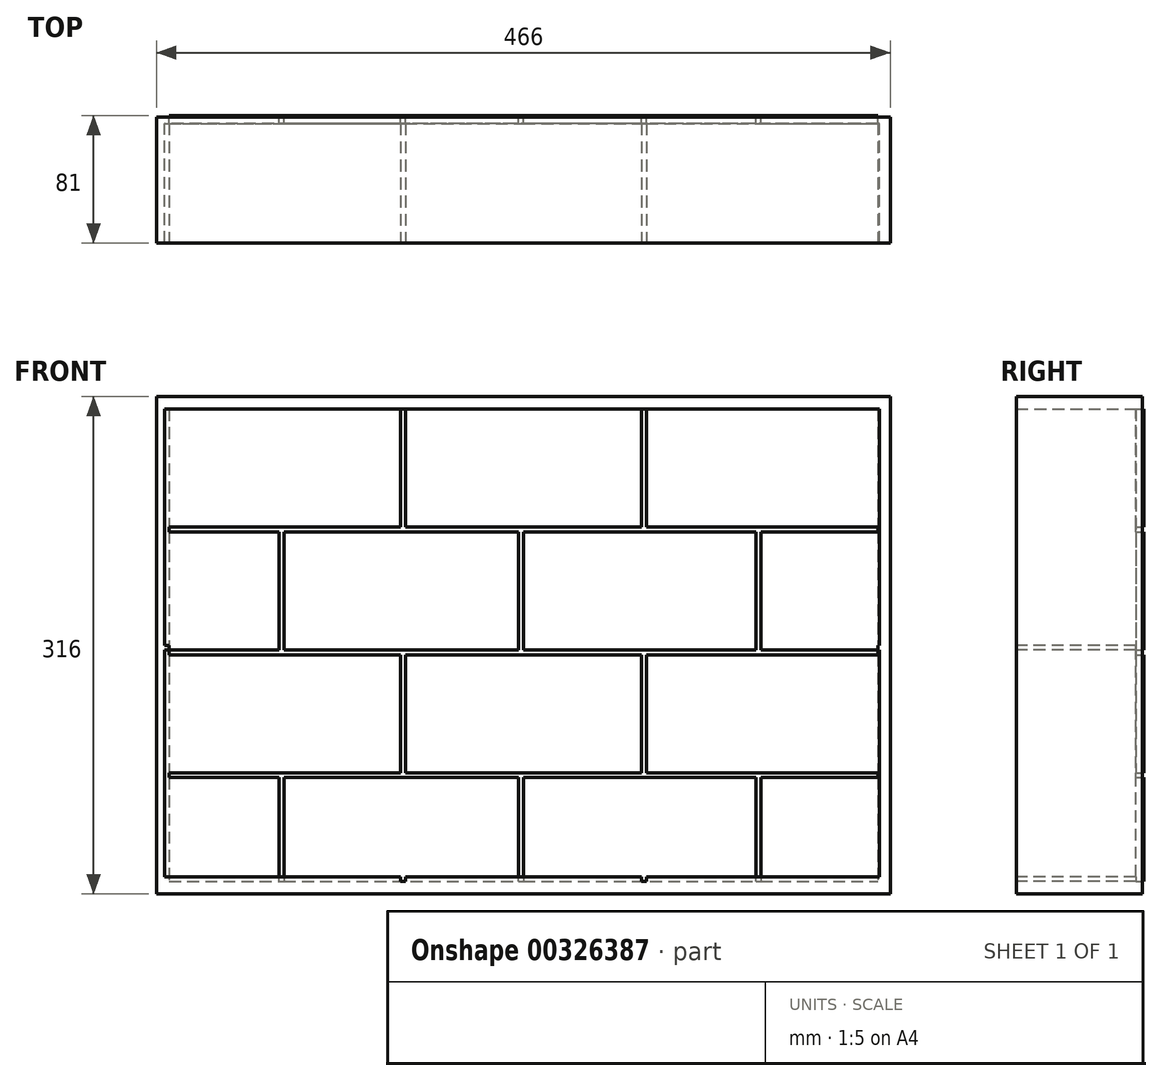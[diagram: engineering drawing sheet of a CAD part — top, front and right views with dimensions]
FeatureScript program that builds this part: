
annotation { "Feature Type Name" : "Feature", "Feature Type Description" : "" }
export const myFeature = defineFeature(function(context is Context, id is Id, definition is map)
    precondition{}
    {
        {
            var Q0;
            Q0=qCreatedBy(makeId("Front.planeOp"),FACE);
            var sketch = newSketch(context, id + "F0", { "sketchPlane" : qUnion([Q0])});
            skLineSegment(sketch, "E0.bottom", {"start": v(0, 300) * mm, "end": v(450, 300) * mm});
            skLineSegment(sketch, "E0.top", {"start": v(0, 0) * mm, "end": v(450, 0) * mm});
            skLineSegment(sketch, "E0.left", {"start": v(0, 300) * mm, "end": v(0, 0) * mm});
            skLineSegment(sketch, "E0.right", {"start": v(450, 300) * mm, "end": v(450, 0) * mm});
            skLineSegment(sketch, "E1.bottom", {"start": v(150, 300) * mm, "end": v(300, 300) * mm});
            skLineSegment(sketch, "E1.top", {"start": v(150, 225) * mm, "end": v(300, 225) * mm});
            skLineSegment(sketch, "E1.left", {"start": v(150, 300) * mm, "end": v(150, 225) * mm});
            skLineSegment(sketch, "E1.right", {"start": v(300, 300) * mm, "end": v(300, 225) * mm});
            skLineSegment(sketch, "E2.bottom", {"start": v(147, 300) * mm, "end": v(0, 300) * mm});
            skLineSegment(sketch, "E2.top", {"start": v(147, 225) * mm, "end": v(0, 225) * mm});
            skLineSegment(sketch, "E2.left", {"start": v(147, 300) * mm, "end": v(147, 225) * mm});
            skLineSegment(sketch, "E2.right", {"start": v(0, 300) * mm, "end": v(0, 225) * mm});
            skLineSegment(sketch, "E3.bottom", {"start": v(303, 300) * mm, "end": v(450, 300) * mm});
            skLineSegment(sketch, "E3.top", {"start": v(303, 225) * mm, "end": v(450, 225) * mm});
            skLineSegment(sketch, "E3.left", {"start": v(303, 300) * mm, "end": v(303, 225) * mm});
            skLineSegment(sketch, "E3.right", {"start": v(450, 300) * mm, "end": v(450, 225) * mm});
            skLineSegment(sketch, "E4", {"start": v(225, 300) * mm, "end": v(225, 0) * mm, "construction": true});
            skLineSegment(sketch, "E5.bottom", {"start": v(72.9, 222) * mm, "end": v(222, 222) * mm});
            skLineSegment(sketch, "E5.top", {"start": v(72.9, 147) * mm, "end": v(222, 147) * mm});
            skLineSegment(sketch, "E5.left", {"start": v(72.9, 222) * mm, "end": v(72.9, 147) * mm});
            skLineSegment(sketch, "E5.right", {"start": v(222, 222) * mm, "end": v(222, 147) * mm});
            skLineSegment(sketch, "E6.bottom", {"start": v(225, 222) * mm, "end": v(372.78, 222) * mm});
            skLineSegment(sketch, "E6.top", {"start": v(225, 147) * mm, "end": v(372.78, 147) * mm});
            skLineSegment(sketch, "E6.left", {"start": v(225, 222) * mm, "end": v(225, 147) * mm});
            skLineSegment(sketch, "E6.right", {"start": v(372.78, 222) * mm, "end": v(372.78, 147) * mm});
            skLineSegment(sketch, "E7.bottom", {"start": v(375.78, 222) * mm, "end": v(450, 222) * mm});
            skLineSegment(sketch, "E7.top", {"start": v(375.78, 147) * mm, "end": v(450, 147) * mm});
            skLineSegment(sketch, "E7.left", {"start": v(375.78, 222) * mm, "end": v(375.78, 147) * mm});
            skLineSegment(sketch, "E7.right", {"start": v(450, 222) * mm, "end": v(450, 147) * mm});
            skLineSegment(sketch, "E8.bottom", {"start": v(0, 222) * mm, "end": v(69.9, 222) * mm});
            skLineSegment(sketch, "E8.top", {"start": v(0, 147) * mm, "end": v(69.9, 147) * mm});
            skLineSegment(sketch, "E8.left", {"start": v(0, 222) * mm, "end": v(0, 147) * mm});
            skLineSegment(sketch, "E8.right", {"start": v(69.9, 222) * mm, "end": v(69.9, 147) * mm});
            skLineSegment(sketch, "E9.bottom", {"start": v(150, 144) * mm, "end": v(300, 144) * mm});
            skLineSegment(sketch, "E9.top", {"start": v(150, 69) * mm, "end": v(300, 69) * mm});
            skLineSegment(sketch, "E9.left", {"start": v(150, 144) * mm, "end": v(150, 69) * mm});
            skLineSegment(sketch, "E9.right", {"start": v(300, 144) * mm, "end": v(300, 69) * mm});
            skLineSegment(sketch, "E10.bottom", {"start": v(303, 144) * mm, "end": v(450, 144) * mm});
            skLineSegment(sketch, "E10.top", {"start": v(303, 69) * mm, "end": v(450, 69) * mm});
            skLineSegment(sketch, "E10.left", {"start": v(303, 144) * mm, "end": v(303, 69) * mm});
            skLineSegment(sketch, "E10.right", {"start": v(450, 144) * mm, "end": v(450, 69) * mm});
            skLineSegment(sketch, "E11.bottom", {"start": v(0, 69) * mm, "end": v(147, 69) * mm});
            skLineSegment(sketch, "E11.top", {"start": v(0, 144) * mm, "end": v(147, 144) * mm});
            skLineSegment(sketch, "E11.left", {"start": v(0, 69) * mm, "end": v(0, 144) * mm});
            skLineSegment(sketch, "E11.right", {"start": v(147, 69) * mm, "end": v(147, 144) * mm});
            skLineSegment(sketch, "E12.bottom", {"start": v(0, 66) * mm, "end": v(69.9, 66) * mm});
            skLineSegment(sketch, "E12.top", {"start": v(0, 0) * mm, "end": v(69.9, 0) * mm});
            skLineSegment(sketch, "E12.left", {"start": v(0, 66) * mm, "end": v(0, 0) * mm});
            skLineSegment(sketch, "E12.right", {"start": v(69.9, 66) * mm, "end": v(69.9, 0) * mm});
            skLineSegment(sketch, "E13.bottom", {"start": v(72.9, 66) * mm, "end": v(222, 66) * mm});
            skLineSegment(sketch, "E13.top", {"start": v(72.9, 0) * mm, "end": v(222, 0) * mm});
            skLineSegment(sketch, "E13.left", {"start": v(72.9, 66) * mm, "end": v(72.9, 0) * mm});
            skLineSegment(sketch, "E13.right", {"start": v(222, 66) * mm, "end": v(222, 0) * mm});
            skLineSegment(sketch, "E14.bottom", {"start": v(225, 66) * mm, "end": v(372.78, 66) * mm});
            skLineSegment(sketch, "E14.top", {"start": v(225, 0) * mm, "end": v(372.78, 0) * mm});
            skLineSegment(sketch, "E14.left", {"start": v(225, 66) * mm, "end": v(225, 0) * mm});
            skLineSegment(sketch, "E14.right", {"start": v(372.78, 66) * mm, "end": v(372.78, 0) * mm});
            skLineSegment(sketch, "E15.bottom", {"start": v(375.78, 66) * mm, "end": v(450, 66) * mm});
            skLineSegment(sketch, "E15.top", {"start": v(375.78, 0) * mm, "end": v(450, 0) * mm});
            skLineSegment(sketch, "E15.left", {"start": v(375.78, 66) * mm, "end": v(375.78, 0) * mm});
            skLineSegment(sketch, "E15.right", {"start": v(450, 66) * mm, "end": v(450, 0) * mm});
            skLineSegment(sketch, "E16.bottom", {"start": v(-8, 308) * mm, "end": v(458, 308) * mm});
            skLineSegment(sketch, "E16.top", {"start": v(-8, -8) * mm, "end": v(458, -8) * mm});
            skLineSegment(sketch, "E16.left", {"start": v(-8, 308) * mm, "end": v(-8, -8) * mm});
            skLineSegment(sketch, "E16.right", {"start": v(458, 308) * mm, "end": v(458, -8) * mm});
            skSolve(sketch);
        }
        {
            var Q0;
            Q0=qCreatedBy(makeId("Front.planeOp"),FACE);
            cPlane(context, id + "F1", {"entities" : qUnion([Q0]), "cplaneType" : CPlaneType.OFFSET, "offset" : 78 * mm, "width" : 150 * mm, "height" : 150 * mm});
        }
        {
            var Q0;
            Q0=qCreatedBy(id+"F1.planeOp",FACE);
            var sketch = newSketch(context, id + "F2", { "sketchPlane" : qUnion([Q0])});
            skLineSegment(sketch, "E17.0", {"start": v(-8, 308) * mm, "end": v(-8, -8) * mm});
            skLineSegment(sketch, "E17.1", {"start": v(-8, 308) * mm, "end": v(458, 308) * mm});
            skLineSegment(sketch, "E17.2", {"start": v(458, 308) * mm, "end": v(458, -8) * mm});
            skLineSegment(sketch, "E17.3", {"start": v(-8, -8) * mm, "end": v(458, -8) * mm});
            skLineSegment(sketch, "E18.0", {"start": v(0, 300) * mm, "end": v(450, 300) * mm});
            skLineSegment(sketch, "E18.1", {"start": v(0, 300) * mm, "end": v(0, 0) * mm});
            skLineSegment(sketch, "E18.2", {"start": v(0, 0) * mm, "end": v(450, 0) * mm});
            skLineSegment(sketch, "E18.3", {"start": v(450, 300) * mm, "end": v(450, 0) * mm});
            skSolve(sketch);
        }
        {
            var Q0;
            Q0 = qSketchRegion(id + "F2", true);
            extrude(context, id + "F3", {"entities" : qUnion([Q0]), "depth" : 3 * mm, "offsetDistance" : 25 * mm, "hasSecondDirection" : true, "secondDirectionOppositeDirection" : true, "secondDirectionDepth" : 77 * mm});
        }
        {
            var Q0;
            Q0=qCreatedBy(makeId("Front.planeOp"),FACE);
            var sketch = newSketch(context, id + "F4", { "sketchPlane" : qUnion([Q0])});
            skLineSegment(sketch, "E19.0.0", {"start": v(147, 225) * mm, "end": v(147, 300) * mm});
            skLineSegment(sketch, "E19.0.1", {"start": v(147, 300) * mm, "end": v(0, 300) * mm});
            skLineSegment(sketch, "E19.0.2", {"start": v(0, 300) * mm, "end": v(0, 225) * mm});
            skLineSegment(sketch, "E19.0.3", {"start": v(0, 225) * mm, "end": v(147, 225) * mm});
            skLineSegment(sketch, "E20.0.0", {"start": v(300, 225) * mm, "end": v(300, 300) * mm});
            skLineSegment(sketch, "E20.0.1", {"start": v(300, 300) * mm, "end": v(150, 300) * mm});
            skLineSegment(sketch, "E20.0.2", {"start": v(150, 300) * mm, "end": v(150, 225) * mm});
            skLineSegment(sketch, "E20.0.3", {"start": v(150, 225) * mm, "end": v(300, 225) * mm});
            skLineSegment(sketch, "E21.0.0", {"start": v(450, 300) * mm, "end": v(303, 300) * mm});
            skLineSegment(sketch, "E21.0.1", {"start": v(303, 300) * mm, "end": v(303, 225) * mm});
            skLineSegment(sketch, "E21.0.2", {"start": v(303, 225) * mm, "end": v(450, 225) * mm});
            skLineSegment(sketch, "E21.0.3", {"start": v(450, 225) * mm, "end": v(450, 300) * mm});
            skLineSegment(sketch, "E22.0.0", {"start": v(69.9, 222) * mm, "end": v(0, 222) * mm});
            skLineSegment(sketch, "E22.0.1", {"start": v(0, 222) * mm, "end": v(0, 147) * mm});
            skLineSegment(sketch, "E22.0.2", {"start": v(0, 147) * mm, "end": v(69.9, 147) * mm});
            skLineSegment(sketch, "E22.0.3", {"start": v(69.9, 147) * mm, "end": v(69.9, 222) * mm});
            skLineSegment(sketch, "E23.0.0", {"start": v(72.9, 222) * mm, "end": v(72.9, 147) * mm});
            skLineSegment(sketch, "E23.0.1", {"start": v(72.9, 147) * mm, "end": v(222, 147) * mm});
            skLineSegment(sketch, "E23.0.2", {"start": v(222, 147) * mm, "end": v(222, 222) * mm});
            skLineSegment(sketch, "E23.0.3", {"start": v(222, 222) * mm, "end": v(72.9, 222) * mm});
            skLineSegment(sketch, "E24.0.0", {"start": v(225, 222) * mm, "end": v(225, 147) * mm});
            skLineSegment(sketch, "E24.0.1", {"start": v(225, 147) * mm, "end": v(372.78, 147) * mm});
            skLineSegment(sketch, "E24.0.2", {"start": v(372.78, 147) * mm, "end": v(372.78, 222) * mm});
            skLineSegment(sketch, "E24.0.3", {"start": v(372.78, 222) * mm, "end": v(225, 222) * mm});
            skLineSegment(sketch, "E25.0.0", {"start": v(450, 147) * mm, "end": v(450, 222) * mm});
            skLineSegment(sketch, "E25.0.1", {"start": v(450, 222) * mm, "end": v(375.78, 222) * mm});
            skLineSegment(sketch, "E25.0.2", {"start": v(375.78, 222) * mm, "end": v(375.78, 147) * mm});
            skLineSegment(sketch, "E25.0.3", {"start": v(375.78, 147) * mm, "end": v(450, 147) * mm});
            skLineSegment(sketch, "E26.0.0", {"start": v(450, 69) * mm, "end": v(450, 144) * mm});
            skLineSegment(sketch, "E26.0.1", {"start": v(450, 144) * mm, "end": v(303, 144) * mm});
            skLineSegment(sketch, "E26.0.2", {"start": v(303, 144) * mm, "end": v(303, 69) * mm});
            skLineSegment(sketch, "E26.0.3", {"start": v(303, 69) * mm, "end": v(450, 69) * mm});
            skLineSegment(sketch, "E27.0.0", {"start": v(150, 144) * mm, "end": v(150, 69) * mm});
            skLineSegment(sketch, "E27.0.1", {"start": v(150, 69) * mm, "end": v(300, 69) * mm});
            skLineSegment(sketch, "E27.0.2", {"start": v(300, 69) * mm, "end": v(300, 144) * mm});
            skLineSegment(sketch, "E27.0.3", {"start": v(300, 144) * mm, "end": v(150, 144) * mm});
            skLineSegment(sketch, "E28.0.0", {"start": v(0, 144) * mm, "end": v(0, 69) * mm});
            skLineSegment(sketch, "E28.0.1", {"start": v(0, 69) * mm, "end": v(147, 69) * mm});
            skLineSegment(sketch, "E28.0.2", {"start": v(147, 69) * mm, "end": v(147, 144) * mm});
            skLineSegment(sketch, "E28.0.3", {"start": v(147, 144) * mm, "end": v(0, 144) * mm});
            skLineSegment(sketch, "E29.0.0", {"start": v(222, 0) * mm, "end": v(222, 66) * mm});
            skLineSegment(sketch, "E29.0.1", {"start": v(222, 66) * mm, "end": v(72.9, 66) * mm});
            skLineSegment(sketch, "E29.0.2", {"start": v(72.9, 66) * mm, "end": v(72.9, 0) * mm});
            skLineSegment(sketch, "E29.0.3", {"start": v(72.9, 0) * mm, "end": v(222, 0) * mm});
            skLineSegment(sketch, "E30.0.0", {"start": v(69.9, 0) * mm, "end": v(69.9, 66) * mm});
            skLineSegment(sketch, "E30.0.1", {"start": v(69.9, 66) * mm, "end": v(0, 66) * mm});
            skLineSegment(sketch, "E30.0.2", {"start": v(0, 66) * mm, "end": v(0, 0) * mm});
            skLineSegment(sketch, "E30.0.3", {"start": v(0, 0) * mm, "end": v(69.9, 0) * mm});
            skLineSegment(sketch, "E31.0.0", {"start": v(372.78, 0) * mm, "end": v(372.78, 66) * mm});
            skLineSegment(sketch, "E31.0.1", {"start": v(372.78, 66) * mm, "end": v(225, 66) * mm});
            skLineSegment(sketch, "E31.0.2", {"start": v(225, 66) * mm, "end": v(225, 0) * mm});
            skLineSegment(sketch, "E31.0.3", {"start": v(225, 0) * mm, "end": v(372.78, 0) * mm});
            skLineSegment(sketch, "E32.0.0", {"start": v(450, 66) * mm, "end": v(375.78, 66) * mm});
            skLineSegment(sketch, "E32.0.1", {"start": v(375.78, 66) * mm, "end": v(375.78, 0) * mm});
            skLineSegment(sketch, "E32.0.2", {"start": v(375.78, 0) * mm, "end": v(450, 0) * mm});
            skLineSegment(sketch, "E32.0.3", {"start": v(450, 0) * mm, "end": v(450, 66) * mm});
            skSolve(sketch);
        }
        {
            var Q0;
            Q0 = qSketchRegion(id + "F4", true);
            extrude(context, id + "F5", {"entities" : qUnion([Q0]), "operationType" : NewBodyOperationType.ADD, "depth" : 5 * mm, "offsetDistance" : 25 * mm});
        }
        {
            var Q0;
            Q0=makeQuery(id+"F3.opExtrude","SWEPT_FACE",FACE,{"disambiguationData":[OSD([sQuery(id+"F2.wireOp",EDGE,"E18.2")])]});
            var sketch = newSketch(context, id + "F6", { "sketchPlane" : qUnion([Q0])});
            skLineSegment(sketch, "E33.0", {"start": v(0, -81) * mm, "end": v(450, -81) * mm, "construction": true});
            skLineSegment(sketch, "E34.bottom", {"start": v(0, -5) * mm, "end": v(147, -5) * mm});
            skLineSegment(sketch, "E34.top", {"start": v(0, -81) * mm, "end": v(147, -81) * mm});
            skLineSegment(sketch, "E34.left", {"start": v(0, -5) * mm, "end": v(0, -81) * mm});
            skLineSegment(sketch, "E34.right", {"start": v(147, -5) * mm, "end": v(147, -81) * mm});
            skLineSegment(sketch, "E35.bottom", {"start": v(150, -5) * mm, "end": v(300, -5) * mm});
            skLineSegment(sketch, "E35.top", {"start": v(150, -81) * mm, "end": v(300, -81) * mm});
            skLineSegment(sketch, "E35.left", {"start": v(150, -5) * mm, "end": v(150, -81) * mm});
            skLineSegment(sketch, "E35.right", {"start": v(300, -5) * mm, "end": v(300, -81) * mm});
            skLineSegment(sketch, "E36.bottom", {"start": v(303, -5) * mm, "end": v(450, -5) * mm});
            skLineSegment(sketch, "E36.top", {"start": v(303, -81) * mm, "end": v(450, -81) * mm});
            skLineSegment(sketch, "E36.left", {"start": v(303, -5) * mm, "end": v(303, -81) * mm});
            skLineSegment(sketch, "E36.right", {"start": v(450, -5) * mm, "end": v(450, -81) * mm});
            skLineSegment(sketch, "E37", {"start": v(225, -81) * mm, "end": v(225, 28.58) * mm, "construction": true});
            skPoint(sketch, "E38", {"position": v(225, -5) * mm});
            skSolve(sketch);
        }
        {
            var Q0;
            Q0 = qSketchRegion(id + "F6", true);
            extrude(context, id + "F7", {"entities" : qUnion([Q0]), "operationType" : NewBodyOperationType.ADD, "depth" : 3 * mm, "offsetDistance" : 25 * mm});
        }
        {
            var Q0;
            Q0=makeQuery(id+"F3.opExtrude","SWEPT_FACE",FACE,{"disambiguationData":[OSD([sQuery(id+"F2.wireOp",EDGE,"E18.1")])]});
            var sketch = newSketch(context, id + "F8", { "sketchPlane" : qUnion([Q0])});
            skLineSegment(sketch, "E39.bottom", {"start": v(-5, 300) * mm, "end": v(-81, 300) * mm});
            skLineSegment(sketch, "E39.top", {"start": v(-5, 150) * mm, "end": v(-81, 150) * mm});
            skLineSegment(sketch, "E39.left", {"start": v(-5, 300) * mm, "end": v(-5, 150) * mm});
            skLineSegment(sketch, "E39.right", {"start": v(-81, 300) * mm, "end": v(-81, 150) * mm});
            skLineSegment(sketch, "E40.bottom", {"start": v(-5, 147) * mm, "end": v(-81, 147) * mm});
            skLineSegment(sketch, "E40.top", {"start": v(-5, 3) * mm, "end": v(-81, 3) * mm});
            skLineSegment(sketch, "E40.left", {"start": v(-5, 147) * mm, "end": v(-5, 3) * mm});
            skLineSegment(sketch, "E40.right", {"start": v(-81, 147) * mm, "end": v(-81, 3) * mm});
            skSolve(sketch);
        }
        {
            var Q0;
            Q0 = qSketchRegion(id + "F8", true);
            extrude(context, id + "F9", {"entities" : qUnion([Q0]), "operationType" : NewBodyOperationType.REMOVE, "oppositeDirection" : true, "depth" : 3 * mm, "offsetDistance" : 25 * mm});
        }
        {
            var Q0;
            Q0=makeQuery(id+"F3.opExtrude","SWEPT_FACE",FACE,{"disambiguationData":[OSD([sQuery(id+"F2.wireOp",EDGE,"E18.3")])]});
            var sketch = newSketch(context, id + "F10", { "sketchPlane" : qUnion([Q0])});
            skLineSegment(sketch, "E41.0", {"start": v(5, 150) * mm, "end": v(5, 300) * mm});
            skLineSegment(sketch, "E42.0", {"start": v(5, 150) * mm, "end": v(81, 150) * mm});
            skPoint(sketch, "E43.orphan", {"position": v(5, 225) * mm});
            skLineSegment(sketch, "E44", {"start": v(5, 300) * mm, "end": v(81, 300) * mm});
            skLineSegment(sketch, "E45", {"start": v(81, 300) * mm, "end": v(81, 150) * mm});
            skLineSegment(sketch, "E46.0", {"start": v(5, 147) * mm, "end": v(81, 147) * mm});
            skLineSegment(sketch, "E47.0", {"start": v(81, 3) * mm, "end": v(5, 3) * mm});
            skLineSegment(sketch, "E48", {"start": v(5, 3) * mm, "end": v(5, 147) * mm});
            skLineSegment(sketch, "E49", {"start": v(81, 147) * mm, "end": v(81, 3) * mm});
            skSolve(sketch);
        }
        {
            var Q0;
            Q0 = qSketchRegion(id + "F10", true);
            extrude(context, id + "F11", {"entities" : qUnion([Q0]), "operationType" : NewBodyOperationType.REMOVE, "oppositeDirection" : true, "depth" : 1 * mm, "offsetDistance" : 25 * mm});
        }
    });
